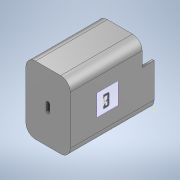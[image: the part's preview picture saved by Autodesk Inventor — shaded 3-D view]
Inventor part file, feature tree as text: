
AUTODESK INVENTOR PART (.ipt)
format: ipt  version: 2022 (Build 260153000, 153)  size: 1,667,072 bytes
history: native  units: in
note: dims shown in document units (in); Inventor stores cm internally (conversion verified against a paired STEP export)
features: sketch x14, extrude x12, fillet x3, shell x1, other x1
ambient origin geometry x8: Origin, YZ Plane, XZ Plane, XY Plane, X Axis, Y Axis, Z Axis, Center Point
bodies: Solid1 (feature_tree)
feature tree (31):
  extrude  "charger"  Depth=1.4567in
  shell  "Shell1"  Thickness=2.7559in
  fillet  "side curve"  Radius=0.1181in
  extrude  "side hole 1"  Depth=0.315in
  extrude  "side hole 2"  TaperAngle=0.0deg  [1 undecoded]
  fillet  "side hole curve"  [1 undecoded]
  extrude  "holder grove"  Depth=0.0197in TaperAngle=0.0deg
  fillet  "Fillet5"  Radius=0.9843in
  extrude  "Type C hole"  TaperAngle=0.0deg  [1 undecoded]
  extrude  "pine hole1"  TaperAngle=0.0deg  [1 undecoded]
  extrude  "insertion wall 1"  Depth=0.2756in
  extrude  "insertion wall 2"  TaperAngle=0.0deg  [1 undecoded]
  extrude  "closer intrussion 1"  Depth=0.1063in
  extrude  "closer intrussion 2"  Depth=0.3937in
  extrude  "closer intrussion 3"  Depth=0.7874in TaperAngle=0.0deg
  extrude  "pcb groove"  Depth=0.0984in
  sketch  "Sketch25"  dims[d36=0.1181in d37=0.0984in]
  sketch  "Sketch26"  dims[d38=0.0787in]
  sketch  "Sketch27"  dims[d39=1.0in d40=0.0in d41=0.1181in d42=0.1181in d43=0.0984in d44=0.0in d45=0.1181in d46=0.0591in d47=0.0591in d48=0.0591in d49=0.0591in d50=0.0984in d51=0.0in d52=0.0984in d53=0.0in d54=0.0984in d55=0.0in d58=0.0709in d59=0.0925in d60=2.638in d61=0.0591in d62=0.0in d63=0.0in d77=2.1094in d78=0.5906in d79=1.2827in d80=2.1685in d81=0.3937in]
  sketch  "Sketch1"  dims[d0=2.2276in d1=1.4567in d2=2.7559in d3=0.0in d4=0.1181in]
  sketch  "Sketch3"  dims[d5=0.315in d8=0.1969in]
  sketch  "Sketch6"  dims[d9=0.1378in d10=0.0in d11=0.0in]
  sketch  "Sketch7"  dims[d12=0.0197in d13=0.0in d15=0.0197in d16=0.0in d18=0.9843in]
  sketch  "Sketch8"  dims[d19=0.0in d20=0.0in]
  sketch  "Sketch10"  dims[d21=0.2953in d22=0.0in]
  sketch  "Sketch11"  dims[d23=0.0394in d24=0.0in d25=0.2756in]
  sketch  "Sketch12"  dims[d26=0.0in d27=0.0in]
  sketch  "Sketch13"  dims[d28=0.1063in d29=0.2339in]
  sketch  "Sketch14"  dims[d30=0.1575in d31=0.0in d32=0.3937in]
  sketch  "Sketch17"  dims[d33=0.7874in d34=0.1575in d35=0.0in]
  other  "Image2"
note: 5 required parameter values undecoded (feature->parameter linkage not recoverable at this tier; creation-order binding heuristic only, values carry confidence <= 0.55)
